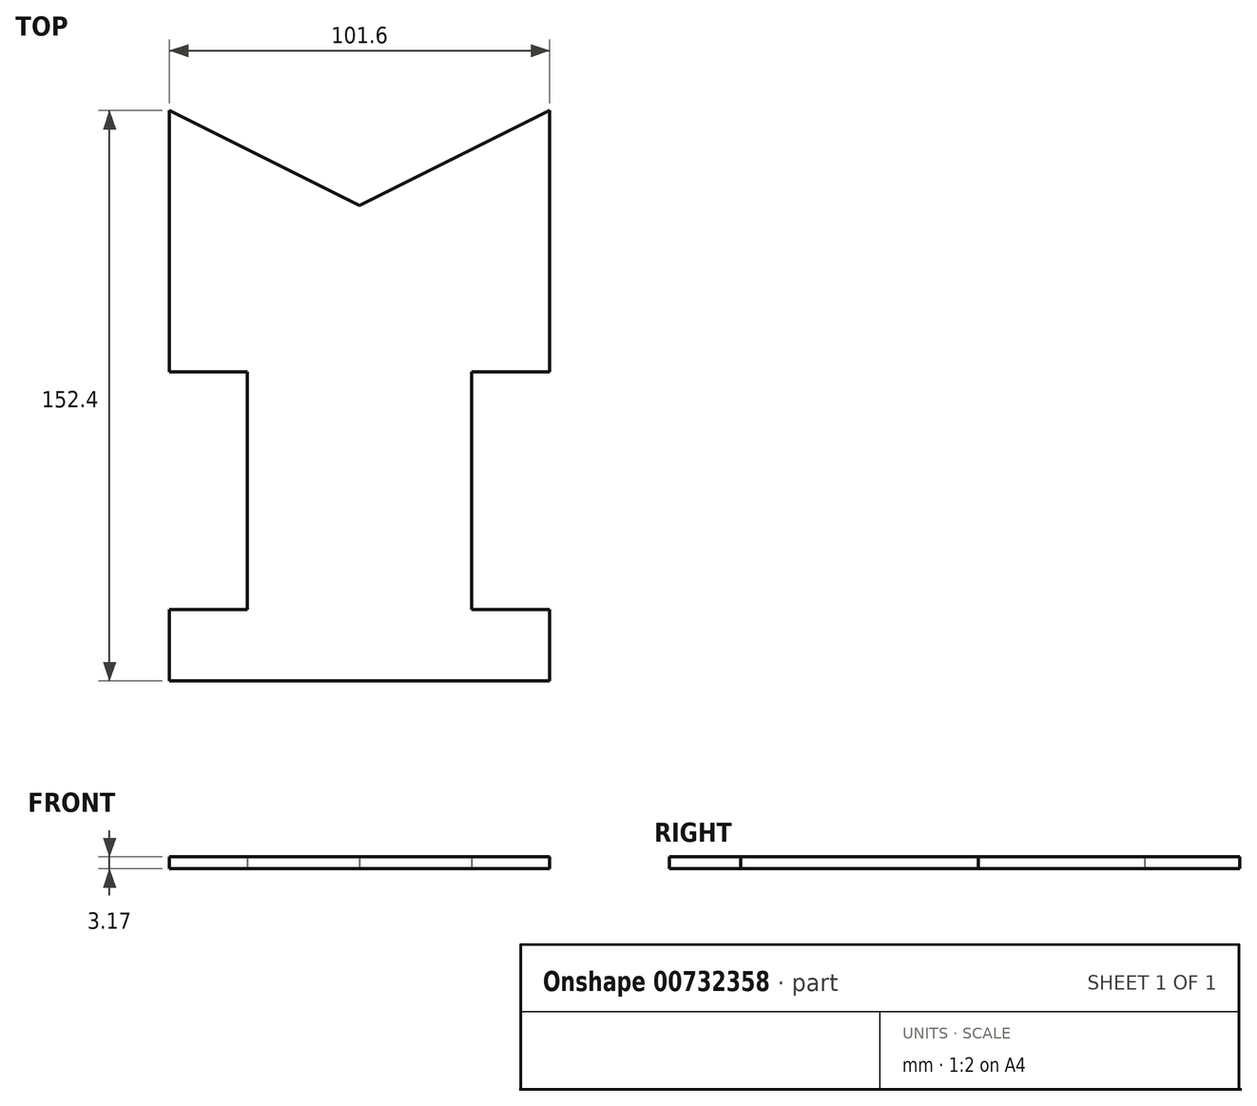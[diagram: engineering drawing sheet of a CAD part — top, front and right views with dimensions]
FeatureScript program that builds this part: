
annotation { "Feature Type Name" : "Feature", "Feature Type Description" : "" }
export const myFeature = defineFeature(function(context is Context, id is Id, definition is map)
    precondition{}
    {
        {
            var Q0;
            Q0=qCreatedBy(makeId("Top.planeOp"),FACE);
            var sketch = newSketch(context, id + "F0", { "sketchPlane" : qUnion([Q0])});
            skLineSegment(sketch, "E0.bottom", {"start": v(50.8, -76.2) * mm, "end": v(-50.8, -76.2) * mm});
            skLineSegment(sketch, "E0.left", {"start": v(50.8, -76.2) * mm, "end": v(50.8, -57.15) * mm});
            skLineSegment(sketch, "E0.right", {"start": v(-50.8, -76.2) * mm, "end": v(-50.8, -57.15) * mm});
            skPoint(sketch, "E0.middle", {"position": v(0, 0) * mm});
            skLineSegment(sketch, "E1", {"start": v(-50.8, 76.2) * mm, "end": v(0, 50.8) * mm});
            skLineSegment(sketch, "E2", {"start": v(50.8, 76.2) * mm, "end": v(0, 50.8) * mm});
            skLineSegment(sketch, "E3.bottom", {"start": v(-50.8, 6.35) * mm, "end": v(-30, 6.35) * mm});
            skLineSegment(sketch, "E3.top", {"start": v(-50.8, -57.15) * mm, "end": v(-30, -57.15) * mm});
            skLineSegment(sketch, "E3.right", {"start": v(-30, 6.35) * mm, "end": v(-30, -57.15) * mm});
            skLineSegment(sketch, "E4.trimOffspring", {"start": v(-50.8, 6.35) * mm, "end": v(-50.8, 76.2) * mm});
            skLineSegment(sketch, "E5.MirrorCS", {"start": v(50.8, 6.35) * mm, "end": v(30, 6.35) * mm});
            skLineSegment(sketch, "E6.MirrorCS", {"start": v(30, 6.35) * mm, "end": v(30, -57.15) * mm});
            skLineSegment(sketch, "E7.MirrorCS", {"start": v(50.8, -57.15) * mm, "end": v(30, -57.15) * mm});
            skLineSegment(sketch, "E8.trimOffspring", {"start": v(50.8, 6.35) * mm, "end": v(50.8, 76.2) * mm});
            skSolve(sketch);
        }
        {
            var Q0;
            Q0=makeQuery(id+"F0.imprint","IMPRINT",FACE,{"disambiguationData":[TD([[makeQuery(id+"F0.imprint","IMPRINT",EDGE,{"derivedFrom":sQuery(id+"F0.wireOp",EDGE,"E0.bottom")}),-1.0]])]});
            extrude(context, id + "F1", {"entities" : qUnion([Q0]), "depth" : 3.17 * mm, "offsetDistance" : 25.4 * mm});
        }
    });
